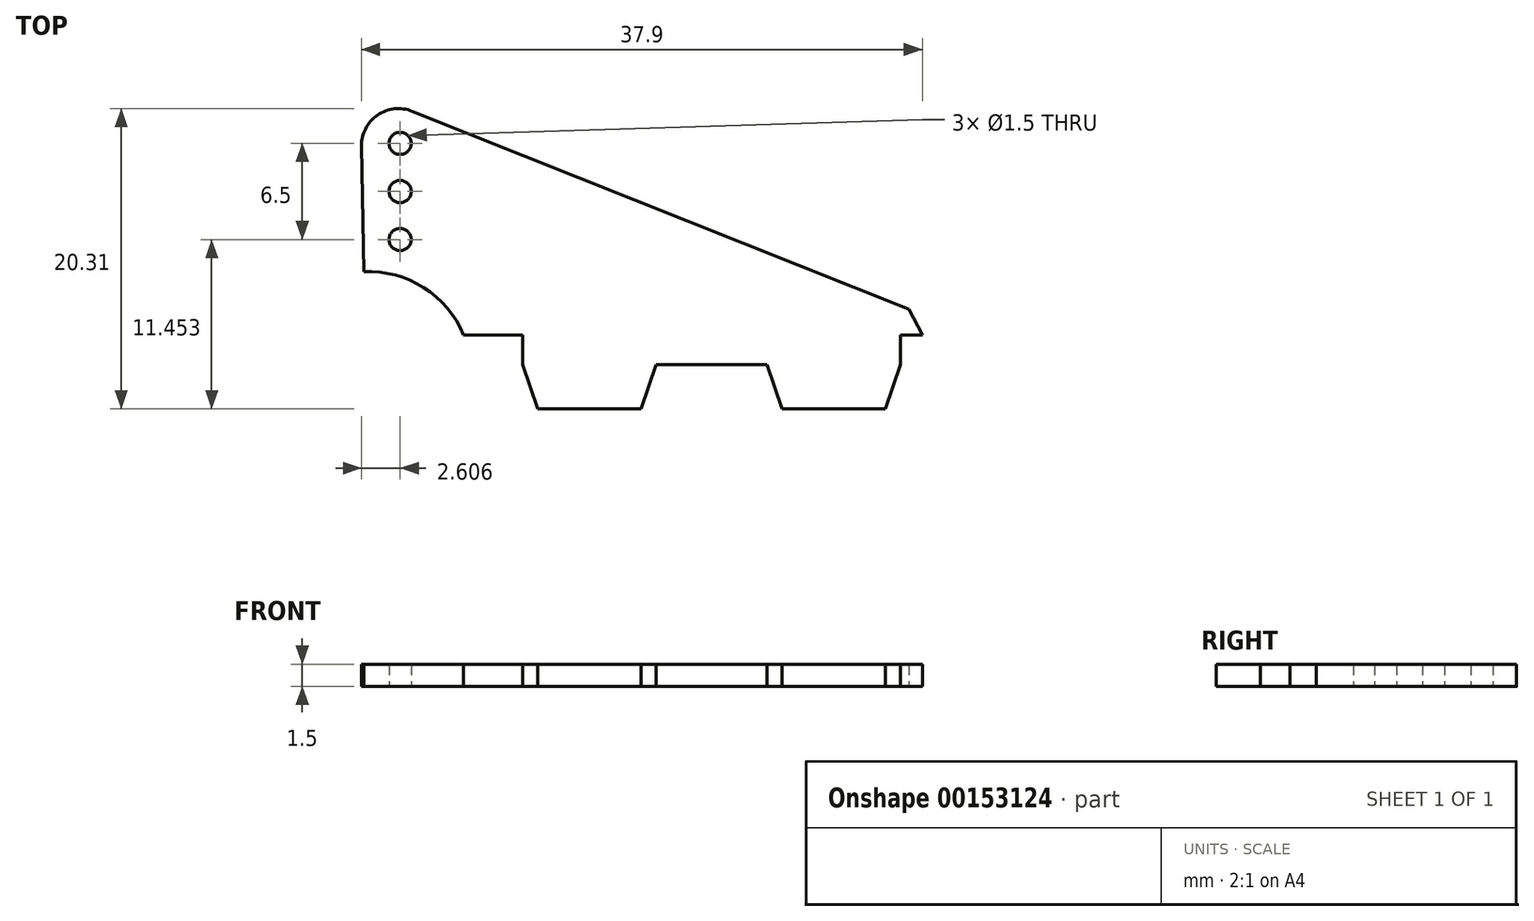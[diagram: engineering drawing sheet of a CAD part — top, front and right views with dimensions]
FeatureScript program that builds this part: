
annotation { "Feature Type Name" : "Feature", "Feature Type Description" : "" }
export const myFeature = defineFeature(function(context is Context, id is Id, definition is map)
    precondition{}
    {
        {
            var Q0;
            Q0=qCreatedBy(makeId("Top.planeOp"),FACE);
            var sketch = newSketch(context, id + "F0", { "sketchPlane" : qUnion([Q0])});
            skLineSegment(sketch, "E0", {"start": v(-26.54, 19.71) * mm, "end": v(4.46, 19.71) * mm, "construction": true});
            skCircle(sketch, "E1", {"center": v(4.46, 19.71) * mm, "radius": 1.5 * mm, "construction": true});
            skCircle(sketch, "E2", {"center": v(-26.54, 19.71) * mm, "radius": 4 * mm, "construction": true});
            skCircle(sketch, "E3", {"center": v(-26.54, 19.71) * mm, "radius": 17 * mm, "construction": true});
            skCircle(sketch, "E4", {"center": v(4.46, 19.71) * mm, "radius": 41 * mm, "construction": true});
            skLineSegment(sketch, "E5", {"start": v(3.56, 21.47) * mm, "end": v(4.46, 19.71) * mm});
            skLineSegment(sketch, "E6", {"start": v(4.46, 19.71) * mm, "end": v(2.96, 19.71) * mm});
            skLineSegment(sketch, "E7", {"start": v(-26.54, 19.71) * mm, "end": v(-22.54, 19.71) * mm});
            skCircle(sketch, "E8", {"center": v(-26.54, 19.71) * mm, "radius": 8 * mm, "construction": true});
            skCircle(sketch, "E9", {"center": v(4.46, 19.71) * mm, "radius": 38 * mm, "construction": true});
            skLineSegment(sketch, "E10", {"start": v(-33.3, 24) * mm, "end": v(-33.44, 32.47) * mm});
            skPoint(sketch, "E11.visualSharp", {"position": v(-33.49, 35.23) * mm});
            skArc(sketch, "E12", {"start": v(-26.54, 19.71) * mm, "mid": v(-29.24, 22.92) * mm, "end": v(-33.3, 24) * mm});
            skLineSegment(sketch, "E13", {"start": v(-22.54, 19.71) * mm, "end": v(-22.54, 17.71) * mm});
            skLineSegment(sketch, "E14", {"start": v(-22.54, 17.71) * mm, "end": v(-22.54, 14.71) * mm, "construction": true});
            skLineSegment(sketch, "E15", {"start": v(-22.54, 14.71) * mm, "end": v(8.64, 14.71) * mm, "construction": true});
            skLineSegment(sketch, "E16", {"start": v(2.96, 19.71) * mm, "end": v(2.96, 17.71) * mm});
            skLineSegment(sketch, "E17", {"start": v(2.96, 17.71) * mm, "end": v(1.96, 17.71) * mm, "construction": true});
            skLineSegment(sketch, "E18", {"start": v(1.96, 17.71) * mm, "end": v(1.96, 13.58) * mm, "construction": true});
            skLineSegment(sketch, "E19", {"start": v(2.96, 17.71) * mm, "end": v(1.96, 14.71) * mm});
            skLineSegment(sketch, "E20", {"start": v(1.96, 14.71) * mm, "end": v(-5.04, 14.71) * mm});
            skLineSegment(sketch, "E21", {"start": v(-5.04, 14.71) * mm, "end": v(-5.04, 17.71) * mm, "construction": true});
            skLineSegment(sketch, "E22", {"start": v(-5.04, 17.71) * mm, "end": v(-6.04, 17.71) * mm, "construction": true});
            skLineSegment(sketch, "E23", {"start": v(-5.04, 14.71) * mm, "end": v(-6.04, 17.71) * mm});
            skLineSegment(sketch, "E24", {"start": v(-22.54, 17.71) * mm, "end": v(-21.54, 17.71) * mm, "construction": true});
            skLineSegment(sketch, "E25", {"start": v(-21.54, 17.71) * mm, "end": v(-21.54, 14.71) * mm, "construction": true});
            skLineSegment(sketch, "E26", {"start": v(-22.54, 17.71) * mm, "end": v(-21.54, 14.71) * mm});
            skLineSegment(sketch, "E27", {"start": v(-21.54, 14.71) * mm, "end": v(-14.54, 14.71) * mm});
            skLineSegment(sketch, "E28", {"start": v(-14.54, 14.71) * mm, "end": v(-14.54, 17.71) * mm, "construction": true});
            skLineSegment(sketch, "E29", {"start": v(-14.54, 17.71) * mm, "end": v(-13.54, 17.71) * mm, "construction": true});
            skLineSegment(sketch, "E30", {"start": v(-14.54, 14.71) * mm, "end": v(-13.54, 17.71) * mm});
            skLineSegment(sketch, "E31", {"start": v(-13.54, 17.71) * mm, "end": v(-6.04, 17.71) * mm});
            skLineSegment(sketch, "E32", {"start": v(-33.33, 26.16) * mm, "end": v(-30.83, 26.2) * mm, "construction": true});
            skLineSegment(sketch, "E33", {"start": v(-30.83, 23.66) * mm, "end": v(-30.83, 36.97) * mm, "construction": true});
            skCircle(sketch, "E34", {"center": v(-30.83, 23.66) * mm, "radius": 2.5 * mm, "construction": true});
            skCircle(sketch, "E35", {"center": v(-30.83, 26.16) * mm, "radius": 0.75 * mm});
            skCircle(sketch, "E36", {"center": v(-30.83, 26.16) * mm, "radius": 3.25 * mm, "construction": true});
            skCircle(sketch, "E37", {"center": v(-30.83, 29.41) * mm, "radius": 0.75 * mm});
            skCircle(sketch, "E38", {"center": v(-30.83, 29.41) * mm, "radius": 3.25 * mm, "construction": true});
            skCircle(sketch, "E39", {"center": v(-30.83, 32.66) * mm, "radius": 0.75 * mm});
            skCircle(sketch, "E40", {"center": v(-30.83, 32.66) * mm, "radius": 2.5 * mm, "construction": true});
            skLineSegment(sketch, "E41", {"start": v(3.56, 21.47) * mm, "end": v(-30.02, 34.84) * mm});
            skPoint(sketch, "E42.visualSharp", {"position": v(-33.5, 36.23) * mm});
            skArc(sketch, "E42.filletArc", {"start": v(-30.02, 34.84) * mm, "mid": v(-32.36, 34.57) * mm, "end": v(-33.44, 32.47) * mm});
            skSolve(sketch);
        }
        {
            var Q0;
            Q0=makeQuery(id+"F0.imprint","IMPRINT",FACE,{"disambiguationData":[TD([[makeQuery(id+"F0.imprint","IMPRINT",EDGE,{"derivedFrom":sQuery(id+"F0.wireOp",EDGE,"E5")}),-1.0]])]});
            extrude(context, id + "F1", {"entities" : qUnion([Q0]), "depth" : 1.5 * mm});
        }
    });
